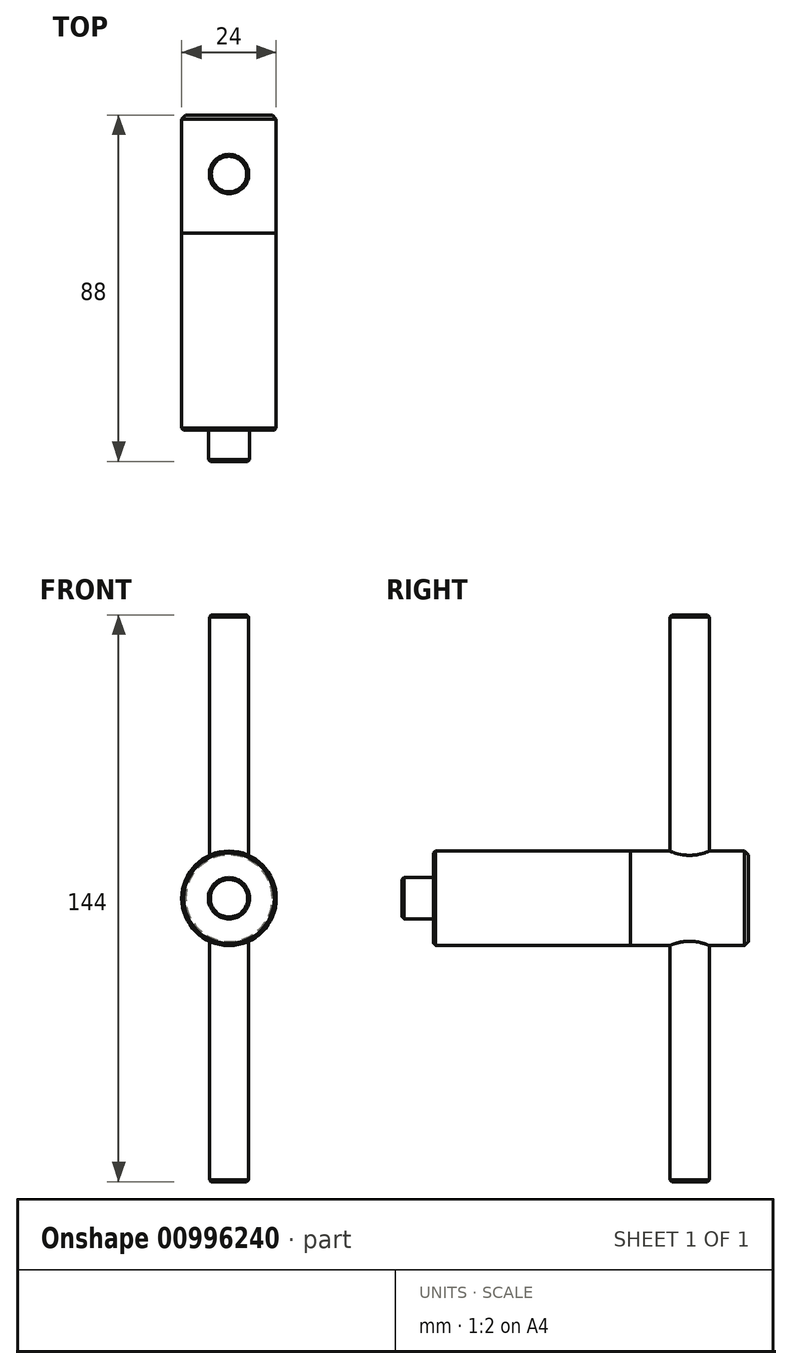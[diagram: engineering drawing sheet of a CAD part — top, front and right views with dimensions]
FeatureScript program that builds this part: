
annotation { "Feature Type Name" : "Feature", "Feature Type Description" : "" }
export const myFeature = defineFeature(function(context is Context, id is Id, definition is map)
    precondition{}
    {
        {
            var Q0;
            Q0=qCreatedBy(makeId("Front.planeOp"),FACE);
            var sketch = newSketch(context, id + "F0", { "sketchPlane" : qUnion([Q0])});
            skCircle(sketch, "E0", {"center": v(0, 0) * mm, "radius": 12 * mm});
            skSolve(sketch);
        }
        {
            var Q0;
            Q0=makeQuery(id+"F0.imprint","IMPRINT",FACE,{"disambiguationData":[TD([[makeQuery(id+"F0.imprint","IMPRINT",EDGE,{"derivedFrom":sQuery(id+"F0.wireOp",EDGE,"E0")}),1.0]])]});
            extrude(context, id + "F1", {"entities" : qUnion([Q0]), "depth" : 20 * mm, "offsetDistance" : 25 * mm});
        }
        {
            var Q0;
            Q0=makeQuery(id+"F1.opExtrude","CAP_FACE",FACE,{"disambiguationData":[OSD([sQuery(id+"F0.wireOp",EDGE,"E0")])],"isStart":false});
            var sketch = newSketch(context, id + "F2", { "sketchPlane" : qUnion([Q0])});
            skCircle(sketch, "E1", {"center": v(0, 0) * mm, "radius": 12 * mm});
            skSolve(sketch);
        }
        {
            var Q0;
            Q0=makeQuery(id+"F2.imprint","IMPRINT",FACE,{"disambiguationData":[TD([[makeQuery(id+"F2.imprint","IMPRINT",EDGE,{"derivedFrom":sQuery(id+"F2.wireOp",EDGE,"E1")}),1.0]])]});
            extrude(context, id + "F3", {"entities" : qUnion([Q0]), "operationType" : NewBodyOperationType.ADD, "depth" : 10 * mm, "offsetDistance" : 25 * mm});
        }
        {
            var Q0;
            Q0=qCreatedBy(makeId("Top.planeOp"),FACE);
            cPlane(context, id + "F4", {"entities" : qUnion([Q0]), "cplaneType" : CPlaneType.OFFSET, "offset" : 12 * mm, "width" : 150 * mm, "height" : 150 * mm});
        }
        {
            var Q0;
            Q0=qCreatedBy(makeId("Top.planeOp"),FACE);
            cPlane(context, id + "F5", {"entities" : qUnion([Q0]), "cplaneType" : CPlaneType.OFFSET, "offset" : 12 * mm, "oppositeDirection" : true, "width" : 150 * mm, "height" : 150 * mm});
        }
        {
            var Q0;
            Q0=qCreatedBy(id+"F4.planeOp",FACE);
            var sketch = newSketch(context, id + "F6", { "sketchPlane" : qUnion([Q0])});
            skCircle(sketch, "E2", {"center": v(0, -15) * mm, "radius": 5 * mm});
            skSolve(sketch);
        }
        {
            var Q0;
            Q0=makeQuery(id+"F6.imprint","IMPRINT",FACE,{"disambiguationData":[TD([[makeQuery(id+"F6.imprint","IMPRINT",EDGE,{"derivedFrom":sQuery(id+"F6.wireOp",EDGE,"E2")}),1.0]])]});
            extrude(context, id + "F7", {"entities" : qUnion([Q0]), "operationType" : NewBodyOperationType.ADD, "depth" : 60 * mm, "offsetDistance" : 25 * mm, "hasSecondDirection" : true, "secondDirectionOppositeDirection" : true, "secondDirectionDepth" : 3 * mm});
        }
        {
            var Q0;
            Q0=qCreatedBy(id+"F5.planeOp",FACE);
            var sketch = newSketch(context, id + "F8", { "sketchPlane" : qUnion([Q0])});
            skCircle(sketch, "E3", {"center": v(0, -15) * mm, "radius": 5 * mm});
            skSolve(sketch);
        }
        {
            var Q0;
            Q0=makeQuery(id+"F8.imprint","IMPRINT",FACE,{"disambiguationData":[TD([[makeQuery(id+"F8.imprint","IMPRINT",EDGE,{"derivedFrom":sQuery(id+"F8.wireOp",EDGE,"E3")}),1.0]])]});
            extrude(context, id + "F9", {"entities" : qUnion([Q0]), "operationType" : NewBodyOperationType.ADD, "oppositeDirection" : true, "depth" : 60 * mm, "offsetDistance" : 25 * mm, "hasSecondDirection" : true, "secondDirectionOppositeDirection" : false, "secondDirectionDepth" : 3 * mm});
        }
        {
            var Q0;
            Q0=makeQuery(id+"F1.opExtrude","CAP_EDGE",EDGE,{"disambiguationData":[OSD([sQuery(id+"F0.wireOp",EDGE,"E0")])],"isStart":true});
            chamfer(context, id + "F10", {"entities" : qUnion([Q0]), "width" : 1 * mm, "tangentPropagation" : true});
        }
        {
            var Q0;
            Q0=makeQuery(id+"F7.opExtrude","CAP_EDGE",EDGE,{"disambiguationData":[OSD([sQuery(id+"F6.wireOp",EDGE,"E2")])],"isStart":false});
            var Q1;
            Q1=makeQuery(id+"F9.opExtrude","CAP_EDGE",EDGE,{"disambiguationData":[OSD([sQuery(id+"F8.wireOp",EDGE,"E3")])],"isStart":false});
            var Q2;
            Q2=makeQuery(id+"F1.opExtrude","CAP_EDGE",EDGE,{"disambiguationData":[OSD([sQuery(id+"F0.wireOp",EDGE,"E0")])],"isStart":false});
            chamfer(context, id + "F11", {"entities" : qUnion([Q0, Q1, Q2]), "width" : 0.5 * mm, "tangentPropagation" : true});
        }
        {
            var Q0;
            Q0=makeQuery(id+"F3.opExtrude","CAP_FACE",FACE,{"disambiguationData":[OSD([sQuery(id+"F2.wireOp",EDGE,"E1")])],"isStart":false});
            var sketch = newSketch(context, id + "F12", { "sketchPlane" : qUnion([Q0])});
            skCircle(sketch, "E4", {"center": v(0, 0) * mm, "radius": 12 * mm});
            skSolve(sketch);
        }
        {
            var Q0;
            Q0=makeQuery(id+"F12.imprint","IMPRINT",FACE,{"disambiguationData":[TD([[makeQuery(id+"F12.imprint","IMPRINT",EDGE,{"derivedFrom":sQuery(id+"F12.wireOp",EDGE,"E4")}),1.0]])]});
            extrude(context, id + "F13", {"entities" : qUnion([Q0]), "depth" : 50 * mm, "offsetDistance" : 25 * mm});
        }
        {
            var Q0;
            Q0=makeQuery(id+"F13.opExtrude","CAP_FACE",FACE,{"disambiguationData":[OSD([sQuery(id+"F12.wireOp",EDGE,"E4")])],"isStart":false});
            var sketch = newSketch(context, id + "F14", { "sketchPlane" : qUnion([Q0])});
            skCircle(sketch, "E5", {"center": v(0, 0) * mm, "radius": 5.25 * mm});
            skSolve(sketch);
        }
        {
            var Q0;
            Q0=makeQuery(id+"F14.imprint","IMPRINT",FACE,{"disambiguationData":[TD([[makeQuery(id+"F14.imprint","IMPRINT",EDGE,{"derivedFrom":sQuery(id+"F14.wireOp",EDGE,"E5")}),1.0]])]});
            extrude(context, id + "F15", {"entities" : qUnion([Q0]), "operationType" : NewBodyOperationType.ADD, "depth" : 8 * mm, "offsetDistance" : 25 * mm});
        }
        {
            var Q0;
            Q0=makeQuery(id+"F13.opExtrude","CAP_EDGE",EDGE,{"disambiguationData":[OSD([sQuery(id+"F12.wireOp",EDGE,"E4")])],"isStart":false});
            var Q1;
            Q1=makeQuery(id+"F15.opExtrude","CAP_EDGE",EDGE,{"disambiguationData":[OSD([sQuery(id+"F14.wireOp",EDGE,"E5")])],"isStart":false});
            chamfer(context, id + "F16", {"entities" : qUnion([Q0, Q1]), "width" : 0.5 * mm, "tangentPropagation" : true});
        }
    });
